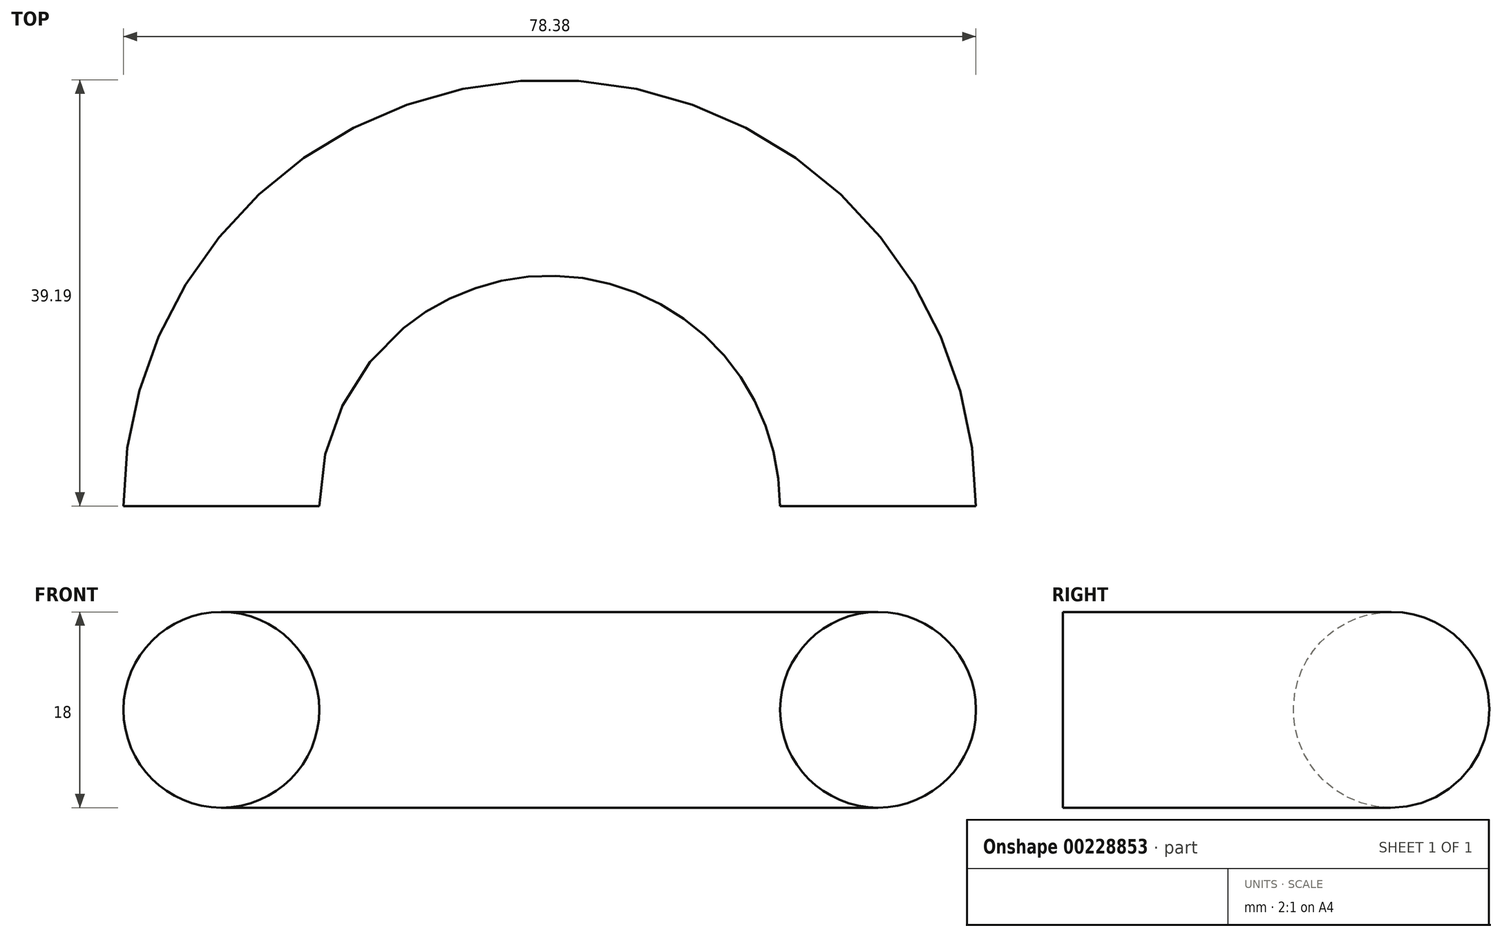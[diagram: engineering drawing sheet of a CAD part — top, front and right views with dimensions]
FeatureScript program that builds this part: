
annotation { "Feature Type Name" : "Feature", "Feature Type Description" : "" }
export const myFeature = defineFeature(function(context is Context, id is Id, definition is map)
    precondition{}
    {
        {
            var Q0;
            Q0=qCreatedBy(makeId("Top.planeOp"),FACE);
            var sketch = newSketch(context, id + "F0", { "sketchPlane" : qUnion([Q0])});
            skLineSegment(sketch, "E0.left", {"start": v(30.18, 29.76) * mm, "end": v(30.18, -29.76) * mm});
            skLineSegment(sketch, "E0.right", {"start": v(-30.18, 29.76) * mm, "end": v(-30.18, -29.76) * mm});
            skPoint(sketch, "E0.middle", {"position": v(0, 0) * mm});
            skArc(sketch, "E1", {"start": v(30.18, 29.76) * mm, "mid": v(0, 59.95) * mm, "end": v(-30.18, 29.76) * mm});
            skArc(sketch, "E2.MirrorCS", {"start": v(30.18, -29.76) * mm, "mid": v(0, -59.95) * mm, "end": v(-30.18, -29.76) * mm});
            skSolve(sketch);
        }
        {
            var Q0;
            Q0=qCreatedBy(makeId("Front.planeOp"),FACE);
            var sketch = newSketch(context, id + "F1", { "sketchPlane" : qUnion([Q0])});
            skPoint(sketch, "E3.2", {"position": v(0, 0) * mm});
            skLineSegment(sketch, "E3.3", {"start": v(-30.18, 0) * mm, "end": v(30.18, 0) * mm});
            skLineSegment(sketch, "E3.4", {"start": v(30.18, 0) * mm, "end": v(-30.18, 0) * mm});
            skCircle(sketch, "E4", {"center": v(-30.18, 0) * mm, "radius": 9 * mm});
            skSolve(sketch);
        }
        {
            var Q0;
            Q0=sQuery(id+"F0.wireOp",VERTEX,"E1.end");
            var Q1;
            Q1=qCreatedBy(makeId("Front.planeOp"),FACE);
            cPlane(context, id + "F2", {"entities" : qUnion([Q0, Q1]), "cplaneType" : CPlaneType.PLANE_POINT, "offset" : 25 * mm, "width" : 150 * mm, "height" : 150 * mm});
        }
        {
            var Q0;
            Q0=qCreatedBy(id+"F2.planeOp",FACE);
            var sketch = newSketch(context, id + "F3", { "sketchPlane" : qUnion([Q0])});
            skCircle(sketch, "E5.0.0", {"center": v(-30.18, 0) * mm, "radius": 9 * mm});
            skSolve(sketch);
        }
        {
            var Q0;
            Q0=makeQuery(id+"F3.imprint","IMPRINT",FACE,{"disambiguationData":[TD([[makeQuery(id+"F3.imprint","IMPRINT",EDGE,{"derivedFrom":sQuery(id+"F3.wireOp",EDGE,"E5.0.0")}),1.0]])]});
            var Q1;
            Q1=sQuery(id+"F0.wireOp",EDGE,"E1");
            sweep(context, id + "F4", {"profiles" : qUnion([Q0]), "path" : qUnion([Q1])});
        }
    });
